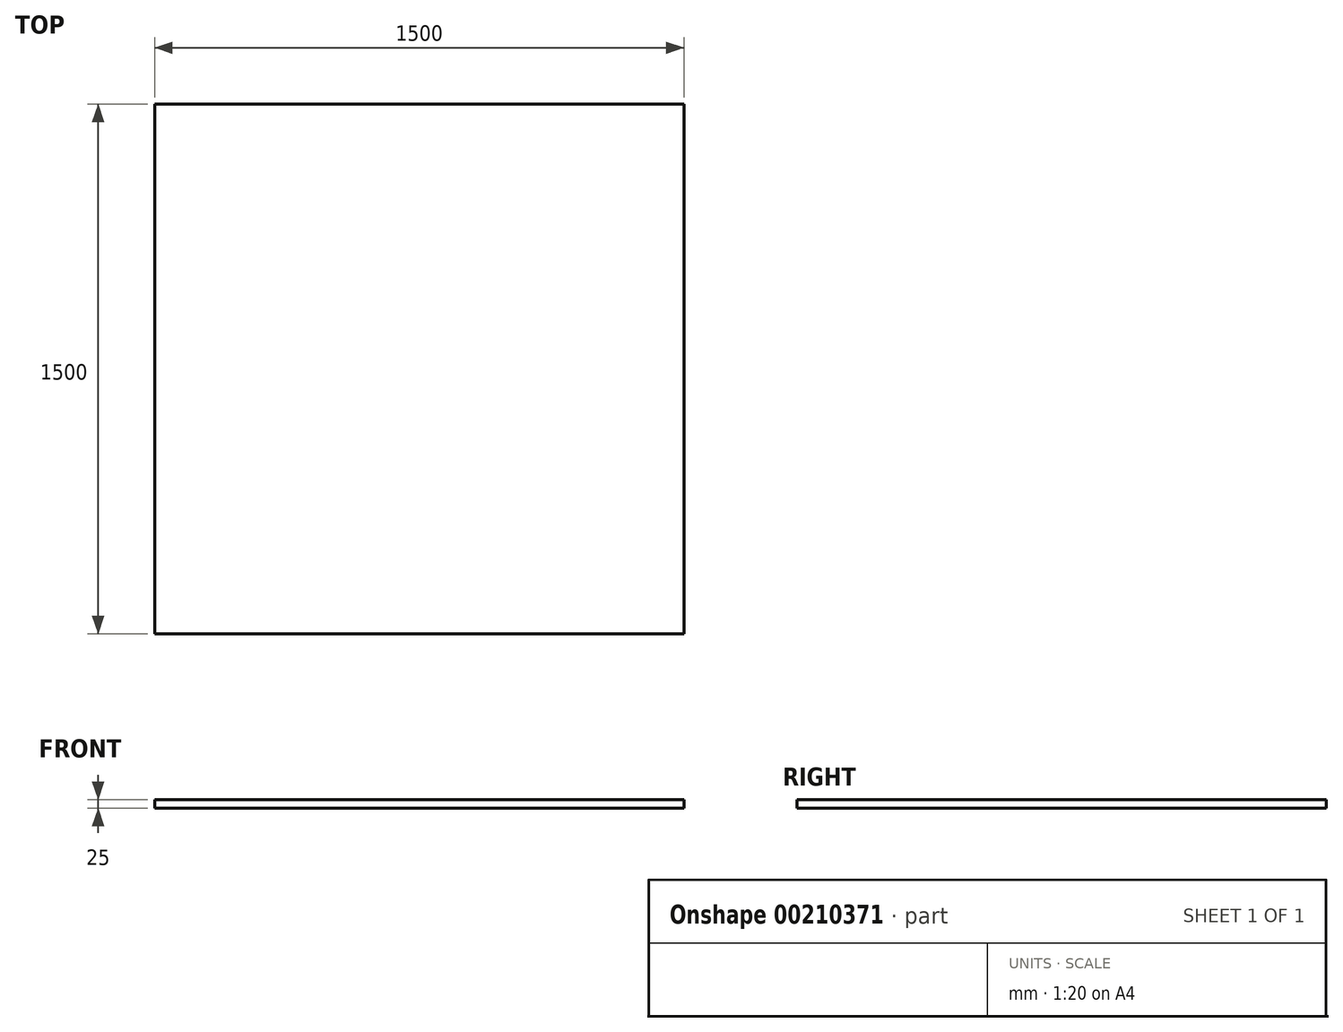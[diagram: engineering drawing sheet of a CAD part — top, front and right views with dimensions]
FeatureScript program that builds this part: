
annotation { "Feature Type Name" : "Feature", "Feature Type Description" : "" }
export const myFeature = defineFeature(function(context is Context, id is Id, definition is map)
    precondition{}
    {
        {
            var Q0;
            Q0=qCreatedBy(makeId("Top.planeOp"),FACE);
            var sketch = newSketch(context, id + "F0", { "sketchPlane" : qUnion([Q0])});
            skLineSegment(sketch, "E0.bottom", {"start": v(-750, 750) * mm, "end": v(750, 750) * mm});
            skLineSegment(sketch, "E0.top", {"start": v(-750, -750) * mm, "end": v(750, -750) * mm});
            skLineSegment(sketch, "E0.left", {"start": v(-750, 750) * mm, "end": v(-750, -750) * mm});
            skLineSegment(sketch, "E0.right", {"start": v(750, 750) * mm, "end": v(750, -750) * mm});
            skPoint(sketch, "E0.middle", {"position": v(0, 0) * mm});
            skSolve(sketch);
        }
        {
            var Q0;
            Q0 = qSketchRegion(id + "F0", true);
            extrude(context, id + "F1", {"entities" : qUnion([Q0]), "depth" : 25 * mm});
        }
    });
